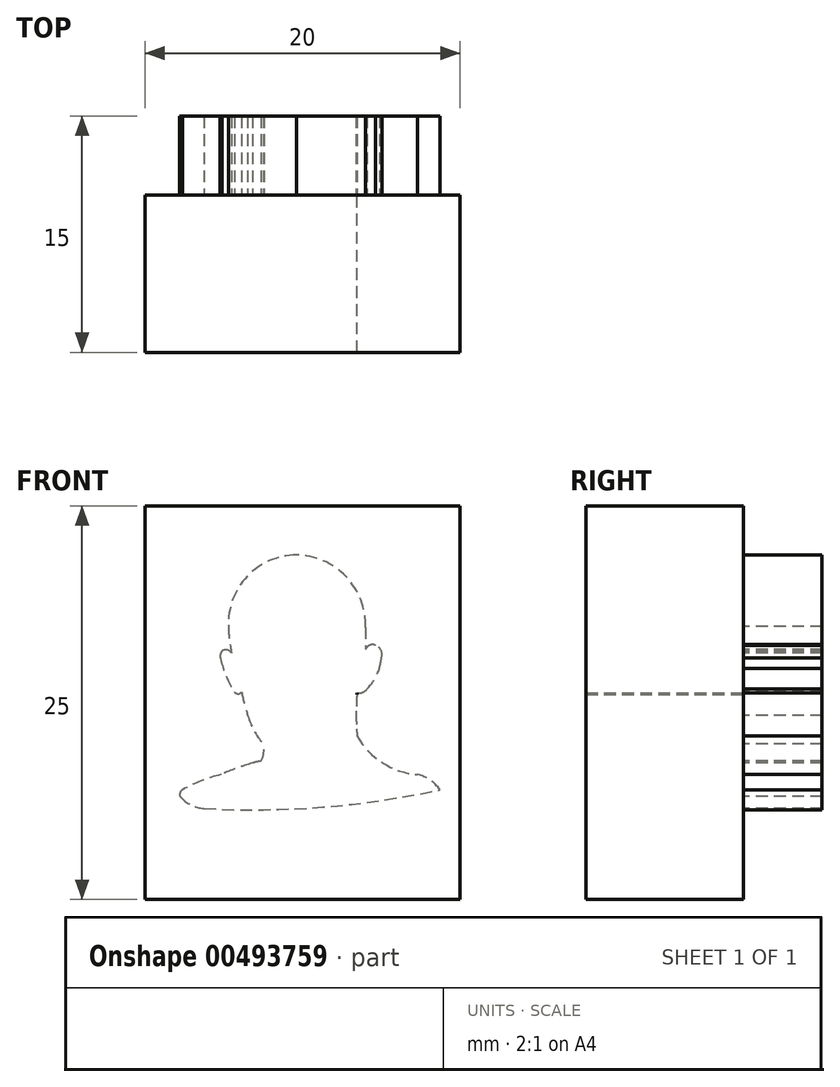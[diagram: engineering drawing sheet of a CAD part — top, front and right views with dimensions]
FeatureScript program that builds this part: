
annotation { "Feature Type Name" : "Feature", "Feature Type Description" : "" }
export const myFeature = defineFeature(function(context is Context, id is Id, definition is map)
    precondition{}
    {
        {
            var Q0;
            Q0=qCreatedBy(makeId("Front.planeOp"),FACE);
            var sketch = newSketch(context, id + "F0", { "sketchPlane" : qUnion([Q0])});
            skLineSegment(sketch, "E0.bottom", {"start": v(10, 12.5) * mm, "end": v(-10, 12.5) * mm});
            skLineSegment(sketch, "E0.top", {"start": v(10, -12.5) * mm, "end": v(-10, -12.5) * mm});
            skLineSegment(sketch, "E0.left", {"start": v(10, 12.5) * mm, "end": v(10, -12.5) * mm});
            skLineSegment(sketch, "E0.right", {"start": v(-10, 12.5) * mm, "end": v(-10, -12.5) * mm});
            skPoint(sketch, "E0.middle", {"position": v(0, 0) * mm});
            skArc(sketch, "E1", {"start": v(-0.4, 9.38) * mm, "mid": v(-3.52, 8.02) * mm, "end": v(-4.7, 4.82) * mm});
            skArc(sketch, "E2", {"start": v(4, 4.78) * mm, "mid": v(2.77, 8) * mm, "end": v(-0.4, 9.38) * mm});
            skArc(sketch, "E3", {"start": v(4, 4.78) * mm, "mid": v(3.99, 4.07) * mm, "end": v(4, 3.37) * mm});
            skArc(sketch, "E4", {"start": v(4.64, 3.64) * mm, "mid": v(4.26, 3.64) * mm, "end": v(4, 3.37) * mm});
            skArc(sketch, "E5", {"start": v(5.02, 2.85) * mm, "mid": v(4.98, 3.32) * mm, "end": v(4.64, 3.64) * mm});
            skArc(sketch, "E6", {"start": v(4.88, 2.16) * mm, "mid": v(4.96, 2.5) * mm, "end": v(5.02, 2.85) * mm});
            skArc(sketch, "E7", {"start": v(4.1, 0.85) * mm, "mid": v(4.56, 1.47) * mm, "end": v(4.88, 2.16) * mm});
            skArc(sketch, "E8", {"start": v(3.47, 0.63) * mm, "mid": v(3.82, 0.65) * mm, "end": v(4.1, 0.85) * mm});
            skArc(sketch, "E9", {"start": v(-4.7, 4.82) * mm, "mid": v(-4.64, 3.99) * mm, "end": v(-4.5, 3.16) * mm});
            skArc(sketch, "E10", {"start": v(-4.5, 3.16) * mm, "mid": v(-4.79, 3.34) * mm, "end": v(-5.12, 3.28) * mm});
            skArc(sketch, "E11", {"start": v(-5.12, 3.28) * mm, "mid": v(-5.22, 3.04) * mm, "end": v(-5.2, 2.77) * mm});
            skArc(sketch, "E12", {"start": v(-5.2, 2.77) * mm, "mid": v(-4.84, 1.68) * mm, "end": v(-4.32, 0.66) * mm});
            skArc(sketch, "E13", {"start": v(-4.32, 0.66) * mm, "mid": v(-4.1, 0.56) * mm, "end": v(-3.87, 0.66) * mm});
            skArc(sketch, "E14", {"start": v(3.14, -0.8) * mm, "mid": v(3.36, -0.1) * mm, "end": v(3.47, 0.63) * mm});
            skArc(sketch, "E15", {"start": v(0.36, -3.83) * mm, "mid": v(2.05, -2.6) * mm, "end": v(3.14, -0.8) * mm});
            skArc(sketch, "E16", {"start": v(-0.81, -3.83) * mm, "mid": v(-0.22, -3.94) * mm, "end": v(0.36, -3.83) * mm});
            skArc(sketch, "E17", {"start": v(-3.48, -0.8) * mm, "mid": v(-2.49, -2.62) * mm, "end": v(-0.81, -3.83) * mm});
            skArc(sketch, "E18", {"start": v(-3.87, 0.66) * mm, "mid": v(-3.7, -0.08) * mm, "end": v(-3.48, -0.8) * mm});
            skArc(sketch, "E19", {"start": v(3.47, 0.63) * mm, "mid": v(3.4, -0.74) * mm, "end": v(3.47, -2.1) * mm});
            skArc(sketch, "E20", {"start": v(3.47, -2.1) * mm, "mid": v(5.08, -3.82) * mm, "end": v(7.31, -4.57) * mm});
            skArc(sketch, "E21", {"start": v(8.73, -5.54) * mm, "mid": v(8.11, -4.92) * mm, "end": v(7.31, -4.57) * mm});
            skArc(sketch, "E22", {"start": v(-6.24, -6.74) * mm, "mid": v(1.28, -6.64) * mm, "end": v(8.73, -5.54) * mm});
            skArc(sketch, "E23", {"start": v(-7.77, -5.97) * mm, "mid": v(-7.08, -6.5) * mm, "end": v(-6.24, -6.74) * mm});
            skArc(sketch, "E24", {"start": v(-7.62, -5.54) * mm, "mid": v(-7.78, -5.73) * mm, "end": v(-7.77, -5.97) * mm});
            skArc(sketch, "E25", {"start": v(-5.18, -4.57) * mm, "mid": v(-6.44, -4.97) * mm, "end": v(-7.62, -5.54) * mm});
            skArc(sketch, "E26", {"start": v(-3.18, -3.83) * mm, "mid": v(-4.2, -4.18) * mm, "end": v(-5.18, -4.57) * mm});
            skArc(sketch, "E27", {"start": v(-2.62, -3.7) * mm, "mid": v(-2.9, -3.77) * mm, "end": v(-3.18, -3.83) * mm});
            skArc(sketch, "E28", {"start": v(-2.62, -3.7) * mm, "mid": v(-2.46, -3.18) * mm, "end": v(-2.49, -2.62) * mm});
            skSolve(sketch);
        }
        {
            var Q0;
            Q0=makeQuery(id+"F0.imprint","IMPRINT",FACE,{"disambiguationData":[TD([[makeQuery(id+"F0.imprint","IMPRINT",EDGE,{"derivedFrom":sQuery(id+"F0.wireOp",EDGE,"E1")}),1.0]])]});
            var Q1;
            {var subQ18=sQuery(id+"F0.wireOp",EDGE,"E15");Q1=makeQuery(id+"F0.imprint","IMPRINT",FACE,{"disambiguationData":[TD([[makeQuery(id+"F0.imprint","IMPRINT",EDGE,{"derivedFrom":subQ18}),-1.0]])]});}
            extrude(context, id + "F1", {"entities" : qUnion([Q0, Q1]), "oppositeDirection" : true, "depth" : 5 * mm});
        }
        {
            var Q0;
            Q0=makeQuery(id+"F0.imprint","IMPRINT",FACE,{"disambiguationData":[TD([[makeQuery(id+"F0.imprint","IMPRINT",EDGE,{"derivedFrom":sQuery(id+"F0.wireOp",EDGE,"E0.bottom")}),1.0]])]});
            var Q1;
            Q1=makeQuery(id+"F0.imprint","IMPRINT",FACE,{"disambiguationData":[TD([[makeQuery(id+"F0.imprint","IMPRINT",EDGE,{"derivedFrom":sQuery(id+"F0.wireOp",EDGE,"E1")}),1.0]])]});
            var Q2;
            {var subQ4=sQuery(id+"F0.wireOp",EDGE,"E15");Q2=makeQuery(id+"F0.imprint","IMPRINT",FACE,{"disambiguationData":[TD([[makeQuery(id+"F0.imprint","IMPRINT",EDGE,{"derivedFrom":subQ4}),-1.0]])]});}
            extrude(context, id + "F2", {"entities" : qUnion([Q0, Q1, Q2]), "operationType" : NewBodyOperationType.ADD, "depth" : 10 * mm});
        }
    });
